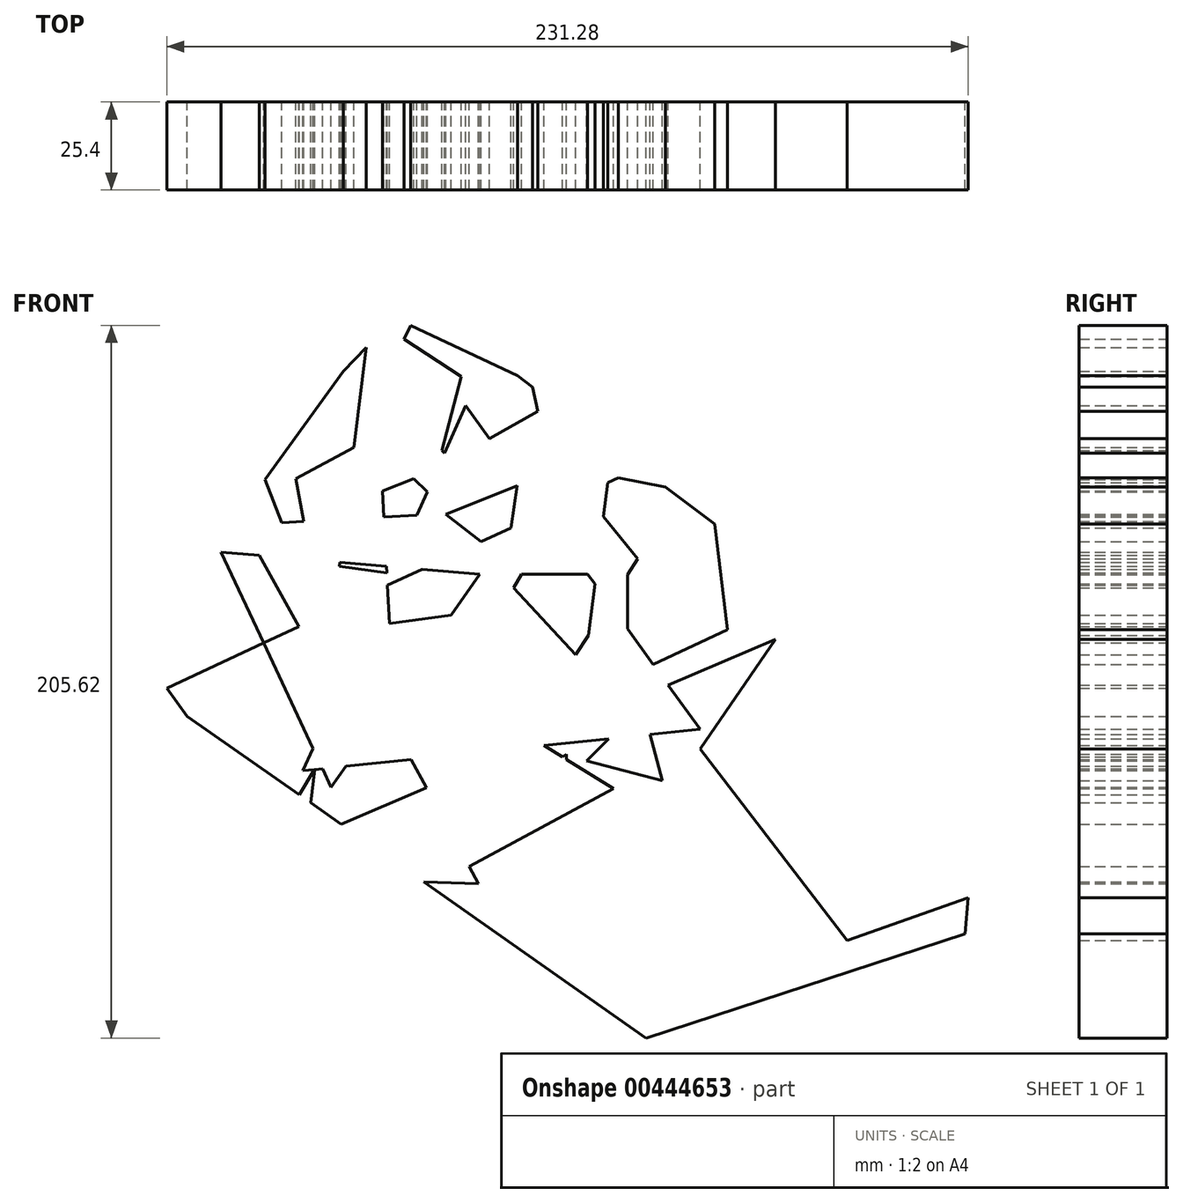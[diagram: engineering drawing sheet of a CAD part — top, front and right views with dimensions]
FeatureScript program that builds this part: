
annotation { "Feature Type Name" : "Feature", "Feature Type Description" : "" }
export const myFeature = defineFeature(function(context is Context, id is Id, definition is map)
    precondition{}
    {
        {
            var Q0;
            Q0=qCreatedBy(makeId("Front.planeOp"),FACE);
            var sketch = newSketch(context, id + "F0", { "sketchPlane" : qUnion([Q0])});
            skLineSegment(sketch, "E0.bottom", {"start": v(0, 0) * mm, "end": v(42.66, 0) * mm});
            skLineSegment(sketch, "E0.top", {"start": v(0, 26.03) * mm, "end": v(42.66, 26.03) * mm});
            skLineSegment(sketch, "E0.left", {"start": v(0, 0) * mm, "end": v(0, 26.03) * mm});
            skLineSegment(sketch, "E0.right", {"start": v(42.66, 0) * mm, "end": v(42.66, 26.03) * mm});
            skCircle(sketch, "E1.cCircle", {"center": v(42.66, 26.03) * mm, "radius": 26.75 * mm, "construction": true});
            skLineSegment(sketch, "E1.0", {"start": v(9.82, 22.06) * mm, "end": v(28.73, 56.02) * mm});
            skLineSegment(sketch, "E1.1", {"start": v(28.73, 56.02) * mm, "end": v(66.88, 48.54) * mm});
            skLineSegment(sketch, "E1.2", {"start": v(66.88, 48.54) * mm, "end": v(71.55, 9.94) * mm});
            skLineSegment(sketch, "E1.3", {"start": v(71.55, 9.94) * mm, "end": v(36.29, -6.42) * mm});
            skLineSegment(sketch, "E1.4", {"start": v(36.29, -6.42) * mm, "end": v(9.82, 22.06) * mm});
            skPoint(sketch, "E1.0.midPoint", {"position": v(19.28, 39.04) * mm});
            skCircle(sketch, "E2.cCircle", {"center": v(7.47, 26.03) * mm, "radius": 47.83 * mm, "construction": true});
            skLineSegment(sketch, "E2.0", {"start": v(-50.02, -50.42) * mm, "end": v(-29.99, 114.04) * mm});
            skLineSegment(sketch, "E2.1", {"start": v(-29.99, 114.04) * mm, "end": v(102.42, 14.46) * mm});
            skLineSegment(sketch, "E2.2", {"start": v(102.42, 14.46) * mm, "end": v(-50.02, -50.42) * mm});
            skPoint(sketch, "E2.0.midPoint", {"position": v(-40, 31.81) * mm});
            skCircle(sketch, "E3.cCircle", {"center": v(-34.12, 44.5) * mm, "radius": 20.96 * mm, "construction": true});
            skLineSegment(sketch, "E3.0", {"start": v(-24.2, 26.03) * mm, "end": v(-48.61, 29.34) * mm});
            skLineSegment(sketch, "E3.1", {"start": v(-48.61, 29.34) * mm, "end": v(-53, 53.6) * mm});
            skLineSegment(sketch, "E3.2", {"start": v(-53, 53.6) * mm, "end": v(-31.3, 65.27) * mm});
            skLineSegment(sketch, "E3.3", {"start": v(-31.3, 65.27) * mm, "end": v(-13.5, 48.23) * mm});
            skLineSegment(sketch, "E3.4", {"start": v(-13.5, 48.23) * mm, "end": v(-24.2, 26.03) * mm});
            skCircle(sketch, "E4.cCircle", {"center": v(-13.44, 41.07) * mm, "radius": 60.01 * mm, "construction": true});
            skLineSegment(sketch, "E4.0", {"start": v(30.32, 0) * mm, "end": v(-38.98, -13.23) * mm});
            skLineSegment(sketch, "E4.1", {"start": v(-38.98, -13.23) * mm, "end": v(-72.98, 48.58) * mm});
            skLineSegment(sketch, "E4.2", {"start": v(-72.98, 48.58) * mm, "end": v(-24.7, 100.02) * mm});
            skLineSegment(sketch, "E4.3", {"start": v(-24.7, 100.02) * mm, "end": v(39.15, 70) * mm});
            skLineSegment(sketch, "E4.4", {"start": v(39.15, 70) * mm, "end": v(30.32, 0) * mm});
            skCircle(sketch, "E5.cCircle", {"center": v(2.88, 8.4) * mm, "radius": 66.55 * mm, "construction": true});
            skLineSegment(sketch, "E5.0", {"start": v(-50.97, -30.72) * mm, "end": v(-4.06, 74.58) * mm});
            skLineSegment(sketch, "E5.1", {"start": v(-4.06, 74.58) * mm, "end": v(63.68, -18.69) * mm});
            skLineSegment(sketch, "E5.2", {"start": v(63.68, -18.69) * mm, "end": v(-50.97, -30.72) * mm});
            skCircle(sketch, "E6.cCircle", {"center": v(-13.66, 0) * mm, "radius": 26.64 * mm, "construction": true});
            skLineSegment(sketch, "E6.0", {"start": v(7.47, 16.21) * mm, "end": v(-10.19, -26.4) * mm});
            skLineSegment(sketch, "E6.1", {"start": v(-10.19, -26.4) * mm, "end": v(-38.27, 10.2) * mm});
            skLineSegment(sketch, "E6.2", {"start": v(-38.27, 10.2) * mm, "end": v(7.47, 16.21) * mm});
            skCircle(sketch, "E7.cCircle", {"center": v(2.88, 41.48) * mm, "radius": 12.76 * mm, "construction": true});
            skLineSegment(sketch, "E7.0", {"start": v(-9.75, 43.29) * mm, "end": v(10.76, 51.52) * mm});
            skLineSegment(sketch, "E7.1", {"start": v(10.76, 51.52) * mm, "end": v(7.64, 29.64) * mm});
            skLineSegment(sketch, "E7.2", {"start": v(7.64, 29.64) * mm, "end": v(-9.75, 43.29) * mm});
            skCircle(sketch, "E8.cCircle", {"center": v(22.14, -31.62) * mm, "radius": 6.32 * mm, "construction": true});
            skLineSegment(sketch, "E8.0", {"start": v(15.82, -31.92) * mm, "end": v(25.03, -26) * mm});
            skLineSegment(sketch, "E8.1", {"start": v(25.03, -26) * mm, "end": v(25.56, -36.94) * mm});
            skLineSegment(sketch, "E8.2", {"start": v(25.56, -36.94) * mm, "end": v(15.82, -31.92) * mm});
            skCircle(sketch, "E9.cCircle", {"center": v(7.47, -34.93) * mm, "radius": 31.22 * mm, "construction": true});
            skLineSegment(sketch, "E9.0", {"start": v(38.68, -35.83) * mm, "end": v(-8.92, -61.5) * mm});
            skLineSegment(sketch, "E9.1", {"start": v(-8.92, -61.5) * mm, "end": v(-7.35, -7.45) * mm});
            skLineSegment(sketch, "E9.2", {"start": v(-7.35, -7.45) * mm, "end": v(38.68, -35.83) * mm});
            skCircle(sketch, "E10.cCircle", {"center": v(43.5, -24.4) * mm, "radius": 13.06 * mm, "construction": true});
            skLineSegment(sketch, "E10.0", {"start": v(46.8, -11.76) * mm, "end": v(52.78, -33.58) * mm});
            skLineSegment(sketch, "E10.1", {"start": v(52.78, -33.58) * mm, "end": v(30.9, -27.85) * mm});
            skLineSegment(sketch, "E10.2", {"start": v(30.9, -27.85) * mm, "end": v(46.8, -11.76) * mm});
            skCircle(sketch, "E11.cCircle", {"center": v(-33.03, -43.19) * mm, "radius": 38.36 * mm, "construction": true});
            skLineSegment(sketch, "E11.0", {"start": v(-32.01, -4.85) * mm, "end": v(-0.33, -63.24) * mm});
            skLineSegment(sketch, "E11.1", {"start": v(-0.33, -63.24) * mm, "end": v(-66.75, -61.48) * mm});
            skLineSegment(sketch, "E11.2", {"start": v(-66.75, -61.48) * mm, "end": v(-32.01, -4.85) * mm});
            skCircle(sketch, "E12.cCircle", {"center": v(-39.18, 7.64) * mm, "radius": 43.28 * mm, "construction": true});
            skLineSegment(sketch, "E12.0", {"start": v(0, 26.03) * mm, "end": v(-42.84, -35.5) * mm});
            skLineSegment(sketch, "E12.1", {"start": v(-42.84, -35.5) * mm, "end": v(-74.7, 32.37) * mm});
            skLineSegment(sketch, "E12.2", {"start": v(-74.7, 32.37) * mm, "end": v(0, 26.03) * mm});
            skCircle(sketch, "E13.cCircle", {"center": v(5.6, 28.25) * mm, "radius": 40.1 * mm, "construction": true});
            skLineSegment(sketch, "E13.0", {"start": v(45.63, 30.45) * mm, "end": v(20.06, -9.15) * mm});
            skLineSegment(sketch, "E13.1", {"start": v(20.06, -9.15) * mm, "end": v(-25.5, 2.93) * mm});
            skLineSegment(sketch, "E13.2", {"start": v(-25.5, 2.93) * mm, "end": v(-28.1, 50) * mm});
            skLineSegment(sketch, "E13.3", {"start": v(-28.1, 50) * mm, "end": v(15.87, 67) * mm});
            skLineSegment(sketch, "E13.4", {"start": v(15.87, 67) * mm, "end": v(45.63, 30.45) * mm});
            skCircle(sketch, "E14.cCircle", {"center": v(-38.03, 70.36) * mm, "radius": 35.14 * mm, "construction": true});
            skLineSegment(sketch, "E14.0", {"start": v(-5.24, 83) * mm, "end": v(-15.88, 43.08) * mm});
            skLineSegment(sketch, "E14.1", {"start": v(-15.88, 43.08) * mm, "end": v(-57.13, 40.87) * mm});
            skLineSegment(sketch, "E14.2", {"start": v(-57.13, 40.87) * mm, "end": v(-71.99, 79.42) * mm});
            skLineSegment(sketch, "E14.3", {"start": v(-71.99, 79.42) * mm, "end": v(-39.91, 105.45) * mm});
            skLineSegment(sketch, "E14.4", {"start": v(-39.91, 105.45) * mm, "end": v(-5.24, 83) * mm});
            skCircle(sketch, "E15.cCircle", {"center": v(-5.24, 83) * mm, "radius": 24.16 * mm, "construction": true});
            skLineSegment(sketch, "E15.0", {"start": v(16.73, 72.95) * mm, "end": v(-8, 59) * mm});
            skLineSegment(sketch, "E15.1", {"start": v(-8, 59) * mm, "end": v(-28.92, 78.22) * mm});
            skLineSegment(sketch, "E15.2", {"start": v(-28.92, 78.22) * mm, "end": v(-17.1, 104.04) * mm});
            skLineSegment(sketch, "E15.3", {"start": v(-17.1, 104.04) * mm, "end": v(11.1, 100.78) * mm});
            skLineSegment(sketch, "E15.4", {"start": v(11.1, 100.78) * mm, "end": v(16.73, 72.95) * mm});
            skCircle(sketch, "E16.cCircle", {"center": v(37.34, 3.76) * mm, "radius": 135.24 * mm, "construction": true});
            skLineSegment(sketch, "E16.0", {"start": v(-97.9, 3.58) * mm, "end": v(-4.62, 132.32) * mm});
            skLineSegment(sketch, "E16.1", {"start": v(-4.62, 132.32) * mm, "end": v(146.64, 83.39) * mm});
            skLineSegment(sketch, "E16.2", {"start": v(146.64, 83.39) * mm, "end": v(146.85, -75.6) * mm});
            skLineSegment(sketch, "E16.3", {"start": v(146.85, -75.6) * mm, "end": v(-4.28, -124.92) * mm});
            skLineSegment(sketch, "E16.4", {"start": v(-4.28, -124.92) * mm, "end": v(-97.9, 3.58) * mm});
            skCircle(sketch, "E17.cCircle", {"center": v(122.92, -22.9) * mm, "radius": 59.28 * mm, "construction": true});
            skLineSegment(sketch, "E17.0", {"start": v(63.65, -24.4) * mm, "end": v(103.17, 33) * mm});
            skLineSegment(sketch, "E17.1", {"start": v(103.17, 33) * mm, "end": v(169.98, 13.16) * mm});
            skLineSegment(sketch, "E17.2", {"start": v(169.98, 13.16) * mm, "end": v(171.75, -56.51) * mm});
            skLineSegment(sketch, "E17.3", {"start": v(171.75, -56.51) * mm, "end": v(106.03, -79.72) * mm});
            skLineSegment(sketch, "E17.4", {"start": v(106.03, -79.72) * mm, "end": v(63.65, -24.4) * mm});
            skCircle(sketch, "E18.cCircle", {"center": v(65, -22.44) * mm, "radius": 159.3 * mm, "construction": true});
            skLineSegment(sketch, "E18.0", {"start": v(-93.68, -8.46) * mm, "end": v(156.45, 108) * mm});
            skLineSegment(sketch, "E18.1", {"start": v(156.45, 108) * mm, "end": v(132.24, -166.85) * mm});
            skLineSegment(sketch, "E18.2", {"start": v(132.24, -166.85) * mm, "end": v(-93.68, -8.46) * mm});
            skSolve(sketch);
        }
        {
            var Q0;
            {var subQ0=sQuery(id+"F0.wireOp",EDGE,"E13.2");var subQ1=sQuery(id+"F0.wireOp",EDGE,"E6.2");var subQ2=makeQuery(id+"F0.imprint","INTERSECT",VERTEX,{"derivedFrom":[subQ1,subQ0]});Q0=makeQuery(id+"F0.imprint","IMPRINT",FACE,{"disambiguationData":[TD([[makeQuery(id+"F0.imprint","IMPRINT",EDGE,{"disambiguationData":[TD([[subQ2,-1.0]])],"derivedFrom":subQ1}),1.0]])]});}
            var Q1;
            {var subQ5=sQuery(id+"F0.wireOp",EDGE,"E0.top");var subQ8=sQuery(id+"F0.wireOp",EDGE,"E1.0");var subQ11=makeQuery(id+"F0.imprint","INTERSECT",VERTEX,{"derivedFrom":[subQ5,subQ8]});Q1=makeQuery(id+"F0.imprint","IMPRINT",FACE,{"disambiguationData":[TD([[makeQuery(id+"F0.imprint","IMPRINT",EDGE,{"disambiguationData":[TD([[subQ11,-1.0]])],"derivedFrom":subQ5}),-1.0]])]});}
            var Q2;
            {var subQ0=sQuery(id+"F0.wireOp",EDGE,"E7.0");Q2=makeQuery(id+"F0.imprint","IMPRINT",FACE,{"disambiguationData":[TD([[makeQuery(id+"F0.imprint","IMPRINT",EDGE,{"derivedFrom":subQ0}),-1.0]])]});}
            var Q3;
            {var subQ0=sQuery(id+"F0.wireOp",EDGE,"E3.0");var subQ1=sQuery(id+"F0.wireOp",EDGE,"E2.0");var subQ2=makeQuery(id+"F0.imprint","INTERSECT",VERTEX,{"derivedFrom":[subQ1,subQ0]});Q3=makeQuery(id+"F0.imprint","IMPRINT",FACE,{"disambiguationData":[TD([[makeQuery(id+"F0.imprint","IMPRINT",EDGE,{"disambiguationData":[TD([[subQ2,-1.0]])],"derivedFrom":subQ1}),-1.0]])]});}
            var Q4;
            {var subQ0=sQuery(id+"F0.wireOp",EDGE,"E13.3");var subQ3=sQuery(id+"F0.wireOp",EDGE,"E3.3");var subQ4=makeQuery(id+"F0.imprint","INTERSECT",VERTEX,{"derivedFrom":[subQ3,subQ0]});Q4=makeQuery(id+"F0.imprint","IMPRINT",FACE,{"disambiguationData":[TD([[makeQuery(id+"F0.imprint","IMPRINT",EDGE,{"disambiguationData":[TD([[subQ4,-1.0]])],"derivedFrom":subQ3}),-1.0]])]});}
            var Q5;
            {var subQ9=sQuery(id+"F0.wireOp",EDGE,"E4.3");var subQ10=sQuery(id+"F0.wireOp",EDGE,"E2.1");var subQ11=makeQuery(id+"F0.imprint","INTERSECT",VERTEX,{"derivedFrom":[subQ10,subQ9]});Q5=makeQuery(id+"F0.imprint","IMPRINT",FACE,{"disambiguationData":[TD([[makeQuery(id+"F0.imprint","IMPRINT",EDGE,{"disambiguationData":[TD([[subQ11,-1.0]])],"derivedFrom":subQ10}),-1.0]])]});}
            var Q6;
            {var subQ0=sQuery(id+"F0.wireOp",EDGE,"E3.2");var subQ3=sQuery(id+"F0.wireOp",EDGE,"E2.0");var subQ4=makeQuery(id+"F0.imprint","INTERSECT",VERTEX,{"derivedFrom":[subQ3,subQ0]});Q6=makeQuery(id+"F0.imprint","IMPRINT",FACE,{"disambiguationData":[TD([[makeQuery(id+"F0.imprint","IMPRINT",EDGE,{"disambiguationData":[TD([[subQ4,-1.0]])],"derivedFrom":subQ3}),1.0]])]});}
            var Q7;
            {var subQ0=sQuery(id+"F0.wireOp",EDGE,"E18.0");var subQ1=sQuery(id+"F0.wireOp",EDGE,"E4.1");var subQ2=makeQuery(id+"F0.imprint","INTERSECT",VERTEX,{"derivedFrom":[subQ1,subQ0]});Q7=makeQuery(id+"F0.imprint","IMPRINT",FACE,{"disambiguationData":[TD([[makeQuery(id+"F0.imprint","IMPRINT",EDGE,{"disambiguationData":[TD([[subQ2,-1.0]])],"derivedFrom":subQ1}),1.0]])]});}
            var Q8;
            {var subQ1=sQuery(id+"F0.wireOp",EDGE,"E2.0");var subQ11=sQuery(id+"F0.wireOp",EDGE,"E18.2");var subQ14=makeQuery(id+"F0.imprint","INTERSECT",VERTEX,{"derivedFrom":[subQ1,subQ11]});Q8=makeQuery(id+"F0.imprint","IMPRINT",FACE,{"disambiguationData":[TD([[makeQuery(id+"F0.imprint","IMPRINT",EDGE,{"disambiguationData":[TD([[subQ14,-1.0]])],"derivedFrom":subQ1}),-1.0]])]});}
            var Q9;
            {var subQ1=sQuery(id+"F0.wireOp",EDGE,"E5.0");var subQ6=sQuery(id+"F0.wireOp",EDGE,"E5.2");var subQ10=makeQuery(id+"F0.imprint","INTERSECT",VERTEX,{"derivedFrom":[subQ1,subQ6]});Q9=makeQuery(id+"F0.imprint","IMPRINT",FACE,{"disambiguationData":[TD([[makeQuery(id+"F0.imprint","IMPRINT",EDGE,{"disambiguationData":[TD([[subQ10,-1.0]])],"derivedFrom":subQ1}),1.0]])]});}
            var Q10;
            {var subQ0=sQuery(id+"F0.wireOp",EDGE,"E10.1");Q10=makeQuery(id+"F0.imprint","IMPRINT",FACE,{"disambiguationData":[TD([[makeQuery(id+"F0.imprint","IMPRINT",EDGE,{"derivedFrom":subQ0}),1.0]])]});}
            var Q11;
            {var subQ3=sQuery(id+"F0.wireOp",EDGE,"E5.1");var subQ7=sQuery(id+"F0.wireOp",EDGE,"E0.right");var subQ8=makeQuery(id+"F0.imprint","INTERSECT",VERTEX,{"derivedFrom":[subQ7,subQ3]});Q11=makeQuery(id+"F0.imprint","IMPRINT",FACE,{"disambiguationData":[TD([[makeQuery(id+"F0.imprint","IMPRINT",EDGE,{"disambiguationData":[TD([[subQ8,-1.0]])],"derivedFrom":subQ7}),-1.0]])]});}
            extrude(context, id + "F1", {"entities" : qUnion([Q0, Q1, Q2, Q3, Q4, Q5, Q6, Q7, Q8, Q9, Q10, Q11]), "depth" : 25.4 * mm});
        }
    });
